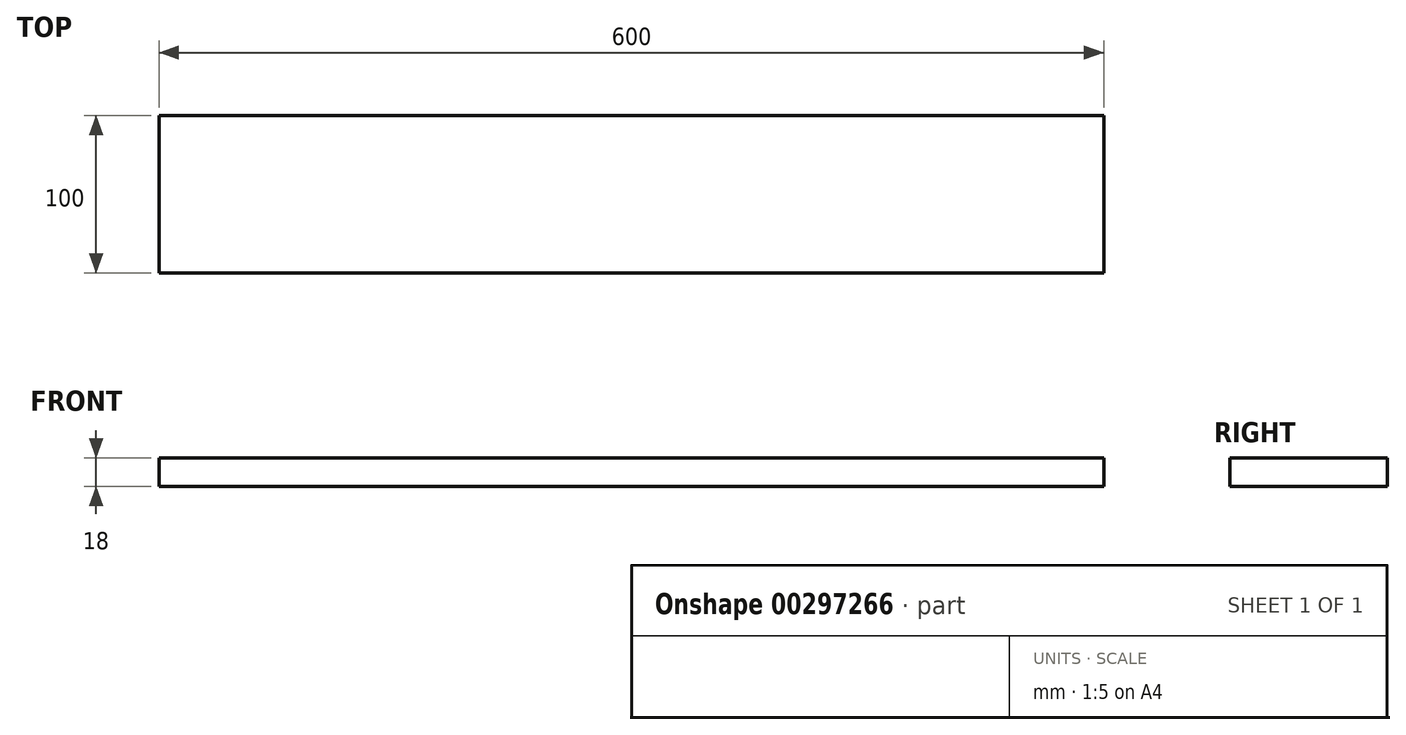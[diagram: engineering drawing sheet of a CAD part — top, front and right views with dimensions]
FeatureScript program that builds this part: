
annotation { "Feature Type Name" : "Feature", "Feature Type Description" : "" }
export const myFeature = defineFeature(function(context is Context, id is Id, definition is map)
    precondition{}
    {
        {
            var Q0;
            Q0=qCreatedBy(makeId("Right.planeOp"),FACE);
            var sketch = newSketch(context, id + "F0", { "sketchPlane" : qUnion([Q0])});
            skLineSegment(sketch, "E0.bottom", {"start": v(50, 9) * mm, "end": v(-50, 9) * mm});
            skLineSegment(sketch, "E0.top", {"start": v(50, -9) * mm, "end": v(-50, -9) * mm});
            skLineSegment(sketch, "E0.left", {"start": v(50, 9) * mm, "end": v(50, -9) * mm});
            skLineSegment(sketch, "E0.right", {"start": v(-50, 9) * mm, "end": v(-50, -9) * mm});
            skPoint(sketch, "E0.middle", {"position": v(0, 0) * mm});
            skSolve(sketch);
        }
        {
            var Q0;
            Q0 = qSketchRegion(id + "F0", true);
            extrude(context, id + "F1", {"entities" : qUnion([Q0]), "depth" : 600 * mm});
        }
    });
